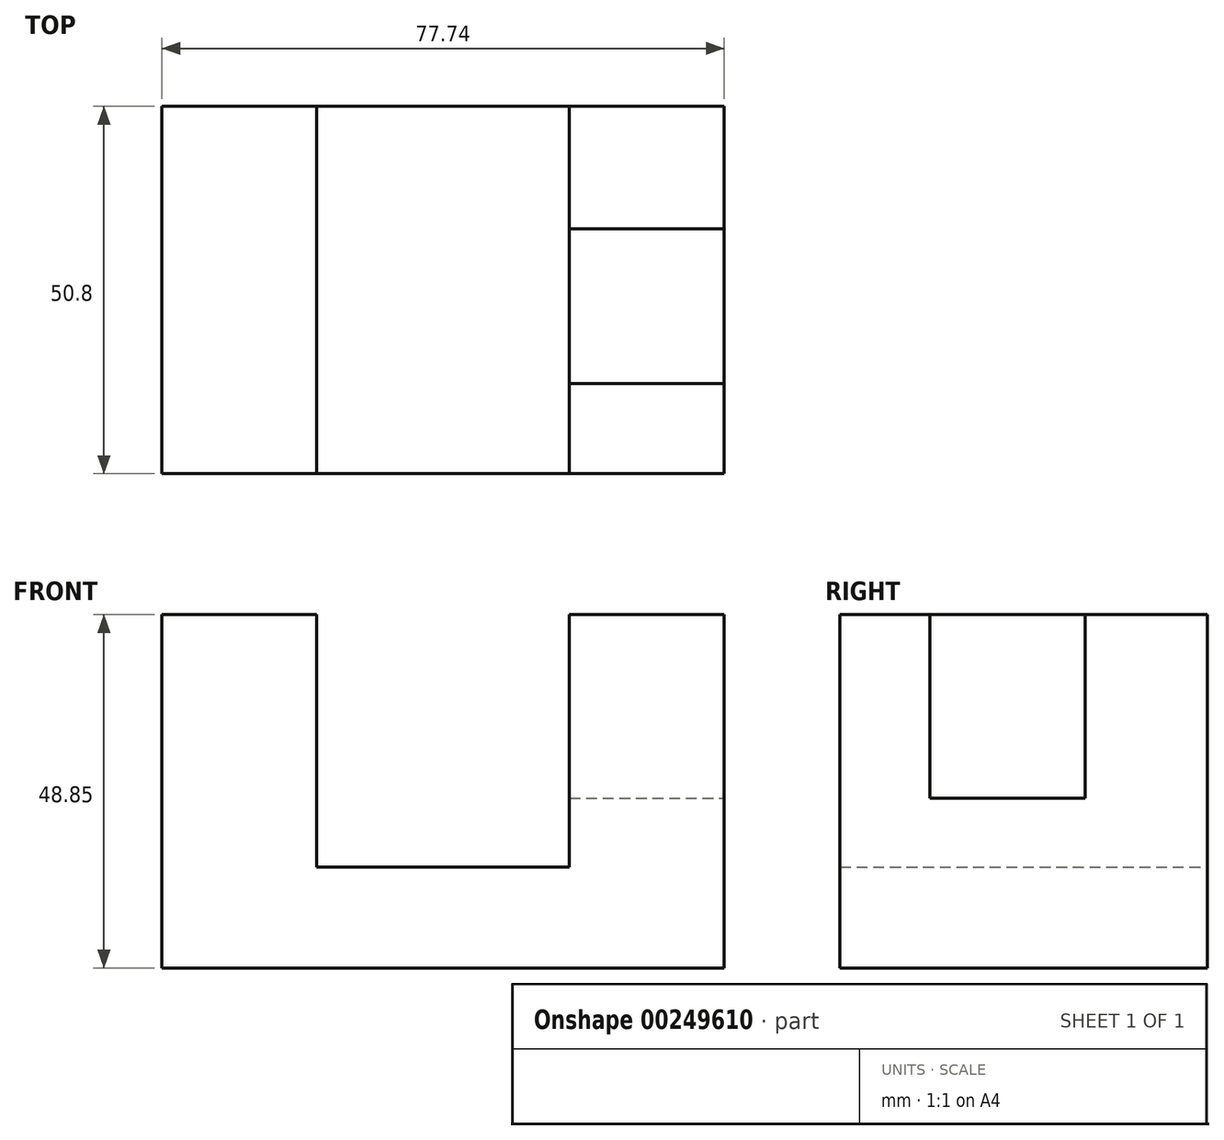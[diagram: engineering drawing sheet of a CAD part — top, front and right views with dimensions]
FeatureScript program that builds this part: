
annotation { "Feature Type Name" : "Feature", "Feature Type Description" : "" }
export const myFeature = defineFeature(function(context is Context, id is Id, definition is map)
    precondition{}
    {
        {
            var Q0;
            Q0=qCreatedBy(makeId("Front.planeOp"),FACE);
            var sketch = newSketch(context, id + "F0", { "sketchPlane" : qUnion([Q0])});
            skLineSegment(sketch, "E0", {"start": v(0, 0) * mm, "end": v(0, 48.85) * mm});
            skLineSegment(sketch, "E1", {"start": v(0, 48.85) * mm, "end": v(21.4, 48.85) * mm});
            skLineSegment(sketch, "E2", {"start": v(77.74, 48.85) * mm, "end": v(77.74, 0) * mm});
            skLineSegment(sketch, "E3", {"start": v(77.74, 0) * mm, "end": v(0, 0) * mm});
            skLineSegment(sketch, "E4", {"start": v(21.4, 48.85) * mm, "end": v(21.4, 13.93) * mm});
            skLineSegment(sketch, "E5", {"start": v(21.4, 13.93) * mm, "end": v(56.33, 13.93) * mm});
            skLineSegment(sketch, "E6", {"start": v(56.33, 13.93) * mm, "end": v(56.33, 48.85) * mm});
            skLineSegment(sketch, "E7.trimOffspring", {"start": v(56.33, 48.85) * mm, "end": v(77.74, 48.85) * mm});
            skSolve(sketch);
        }
        {
            var Q0;
            Q0 = qSketchRegion(id + "F0", true);
            extrude(context, id + "F1", {"entities" : qUnion([Q0]), "depth" : 25.4 * mm, "hasSecondDirection" : true, "secondDirectionOppositeDirection" : true, "secondDirectionDepth" : 25.4 * mm});
        }
        {
            var Q0;
            Q0=makeQuery(id+"F1.opExtrude","SWEPT_FACE",FACE,{"disambiguationData":[OSD([sQuery(id+"F0.wireOp",EDGE,"E7.trimOffspring")])]});
            var sketch = newSketch(context, id + "F2", { "sketchPlane" : qUnion([Q0])});
            skLineSegment(sketch, "E8", {"start": v(56.33, -12.95) * mm, "end": v(77.74, -12.95) * mm});
            skLineSegment(sketch, "E9", {"start": v(56.33, -12.95) * mm, "end": v(56.33, 8.46) * mm});
            skLineSegment(sketch, "E10", {"start": v(56.33, 8.46) * mm, "end": v(77.74, 8.46) * mm});
            skLineSegment(sketch, "E11", {"start": v(77.74, 8.46) * mm, "end": v(77.74, -12.95) * mm});
            skSolve(sketch);
        }
        {
            var Q0;
            Q0 = qSketchRegion(id + "F2", true);
            extrude(context, id + "F3", {"entities" : qUnion([Q0]), "operationType" : NewBodyOperationType.REMOVE, "oppositeDirection" : true, "depth" : 25.4 * mm});
        }
    });
